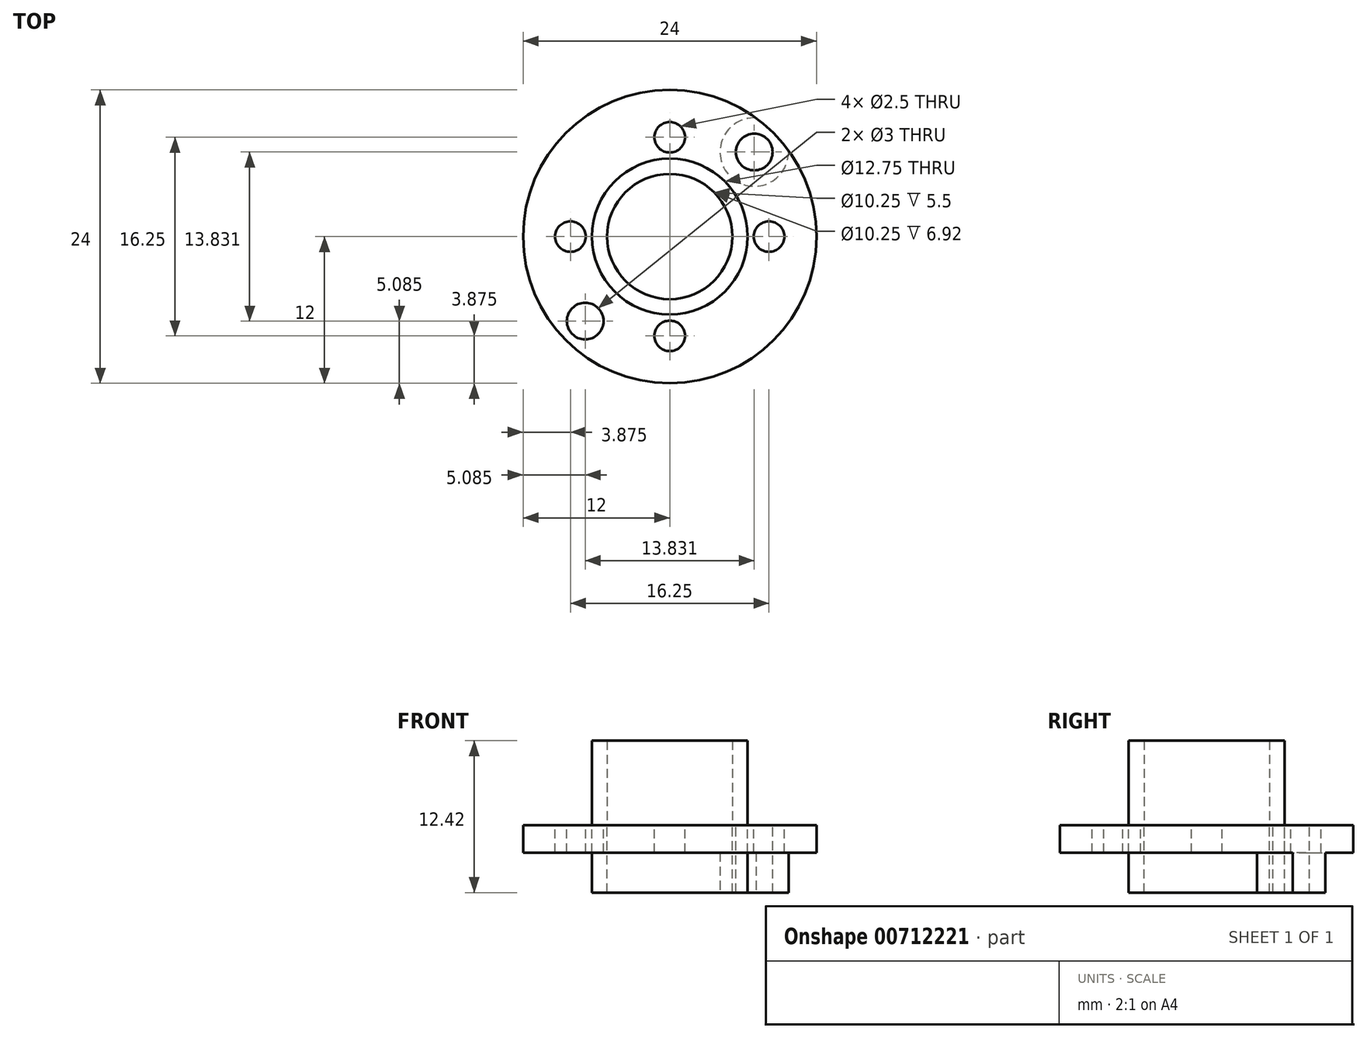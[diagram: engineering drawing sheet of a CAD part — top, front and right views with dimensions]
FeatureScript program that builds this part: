
annotation { "Feature Type Name" : "Feature", "Feature Type Description" : "" }
export const myFeature = defineFeature(function(context is Context, id is Id, definition is map)
    precondition{}
    {
        {
            var Q0;
            Q0=qCreatedBy(makeId("Top.planeOp"),FACE);
            var sketch = newSketch(context, id + "F0", { "sketchPlane" : qUnion([Q0])});
            skCircle(sketch, "E0", {"center": v(0, 0) * mm, "radius": 5.12 * mm});
            skCircle(sketch, "E1", {"center": v(0, 0) * mm, "radius": 6.38 * mm});
            skCircle(sketch, "E2", {"center": v(0, 0) * mm, "radius": 12 * mm});
            skLineSegment(sketch, "E3", {"start": v(-12, 0) * mm, "end": v(12, 0) * mm, "construction": true});
            skCircle(sketch, "E4", {"center": v(-8.12, 0) * mm, "radius": 1.25 * mm});
            skCircle(sketch, "E5.1.0", {"center": v(0, -8.12) * mm, "radius": 1.25 * mm});
            skCircle(sketch, "E5.2.0", {"center": v(8.12, 0) * mm, "radius": 1.25 * mm});
            skCircle(sketch, "E5.3.0", {"center": v(0, 8.12) * mm, "radius": 1.25 * mm});
            skLineSegment(sketch, "E6.1.0", {"start": v(-8.49, -8.49) * mm, "end": v(8.49, 8.49) * mm, "construction": true});
            skLineSegment(sketch, "E6.2.0", {"start": v(0, -12) * mm, "end": v(0, 12) * mm, "construction": true});
            skLineSegment(sketch, "E6.3.0", {"start": v(8.49, -8.49) * mm, "end": v(-8.49, 8.49) * mm, "construction": true});
            skLineSegment(sketch, "E6.4.0", {"start": v(12, 0) * mm, "end": v(-12, 0) * mm, "construction": true});
            skLineSegment(sketch, "E6.5.0", {"start": v(8.49, 8.49) * mm, "end": v(-8.49, -8.49) * mm, "construction": true});
            skLineSegment(sketch, "E6.6.0", {"start": v(0, 12) * mm, "end": v(0, -12) * mm, "construction": true});
            skLineSegment(sketch, "E6.7.0", {"start": v(-8.49, 8.49) * mm, "end": v(8.49, -8.49) * mm, "construction": true});
            skCircle(sketch, "E7", {"center": v(6.92, 6.92) * mm, "radius": 1.5 * mm});
            skCircle(sketch, "E8.MirrorC", {"center": v(-6.92, -6.92) * mm, "radius": 1.5 * mm});
            skSolve(sketch);
        }
        {
            var Q0;
            Q0=makeQuery(id+"F0.imprint","IMPRINT",FACE,{"disambiguationData":[TD([[makeQuery(id+"F0.imprint","IMPRINT",EDGE,{"derivedFrom":sQuery(id+"F0.wireOp",EDGE,"E0")}),-1.0]])]});
            extrude(context, id + "F1", {"entities" : qUnion([Q0]), "depth" : 6.92 * mm, "offsetDistance" : 25 * mm});
        }
        {
            var Q0;
            Q0 = qSketchRegion(id + "F0", true);
            extrude(context, id + "F2", {"entities" : qUnion([Q0]), "oppositeDirection" : true, "depth" : 5.5 * mm, "offsetDistance" : 25 * mm});
        }
        {
            var Q0;
            Q0=makeQuery(id+"F2.opExtrude","CAP_FACE",FACE,{"disambiguationData":[OSD([sQuery(id+"F0.wireOp",EDGE,"E1"),sQuery(id+"F0.wireOp",EDGE,"E2"),sQuery(id+"F0.wireOp",EDGE,"E4"),sQuery(id+"F0.wireOp",EDGE,"E5.1.0"),sQuery(id+"F0.wireOp",EDGE,"E5.2.0"),sQuery(id+"F0.wireOp",EDGE,"E5.3.0"),sQuery(id+"F0.wireOp",EDGE,"E7"),sQuery(id+"F0.wireOp",EDGE,"E8.MirrorC")])],"isStart":false});
            cPlane(context, id + "F3", {"entities" : qUnion([Q0]), "cplaneType" : CPlaneType.OFFSET, "offset" : 0 * mm, "width" : 150 * mm, "height" : 150 * mm});
        }
        {
            var Q0;
            Q0=qCreatedBy(id+"F3.planeOp",FACE);
            var sketch = newSketch(context, id + "F4", { "sketchPlane" : qUnion([Q0])});
            skCircle(sketch, "E9", {"center": v(0, 0) * mm, "radius": 5.12 * mm});
            skCircle(sketch, "E10", {"center": v(0, 0) * mm, "radius": 12 * mm});
            skLineSegment(sketch, "E11", {"start": v(0, 0) * mm, "end": v(-12, 0) * mm, "construction": true});
            skLineSegment(sketch, "E12.1.0", {"start": v(0, 0) * mm, "end": v(-8.49, -8.49) * mm, "construction": true});
            skLineSegment(sketch, "E12.2.0", {"start": v(0, 0) * mm, "end": v(0, -12) * mm, "construction": true});
            skLineSegment(sketch, "E12.3.0", {"start": v(0, 0) * mm, "end": v(8.49, -8.49) * mm, "construction": true});
            skLineSegment(sketch, "E12.4.0", {"start": v(0, 0) * mm, "end": v(12, 0) * mm, "construction": true});
            skLineSegment(sketch, "E12.5.0", {"start": v(0, 0) * mm, "end": v(8.49, 8.49) * mm, "construction": true});
            skLineSegment(sketch, "E12.6.0", {"start": v(0, 0) * mm, "end": v(0, 12) * mm, "construction": true});
            skLineSegment(sketch, "E12.7.0", {"start": v(0, 0) * mm, "end": v(-8.49, 8.49) * mm, "construction": true});
            skArc(sketch, "E13", {"start": v(-9.71, 7.05) * mm, "mid": v(-4.94, 4.94) * mm, "end": v(-7.05, 9.71) * mm});
            skArc(sketch, "E14.MirrorC", {"start": v(7.05, -9.71) * mm, "mid": v(4.94, -4.94) * mm, "end": v(9.71, -7.05) * mm});
            skSolve(sketch);
        }
        {
            var Q0;
            {var subQ0=sQuery(id+"F4.wireOp",EDGE,"E13");Q0=makeQuery(id+"F4.imprint","IMPRINT",FACE,{"disambiguationData":[TD([[makeQuery(id+"F4.imprint","IMPRINT",EDGE,{"derivedFrom":subQ0}),1.0]])]});}
            var Q1;
            {var subQ0=sQuery(id+"F4.wireOp",EDGE,"E14.MirrorC");Q1=makeQuery(id+"F4.imprint","IMPRINT",FACE,{"disambiguationData":[TD([[makeQuery(id+"F4.imprint","IMPRINT",EDGE,{"derivedFrom":subQ0}),-1.0]])]});}
            extrude(context, id + "F5", {"entities" : qUnion([Q0, Q1]), "operationType" : NewBodyOperationType.REMOVE, "oppositeDirection" : true, "depth" : 3.27 * mm, "offsetDistance" : 25 * mm});
        }
        {
            var Q0;
            Q0=makeQuery(id+"F0.imprint","IMPRINT",FACE,{"disambiguationData":[TD([[makeQuery(id+"F0.imprint","IMPRINT",EDGE,{"derivedFrom":sQuery(id+"F0.wireOp",EDGE,"E0")}),-1.0]])]});
            extrude(context, id + "F6", {"entities" : qUnion([Q0]), "oppositeDirection" : true, "depth" : 5.5 * mm, "offsetDistance" : 25 * mm});
        }
    });
